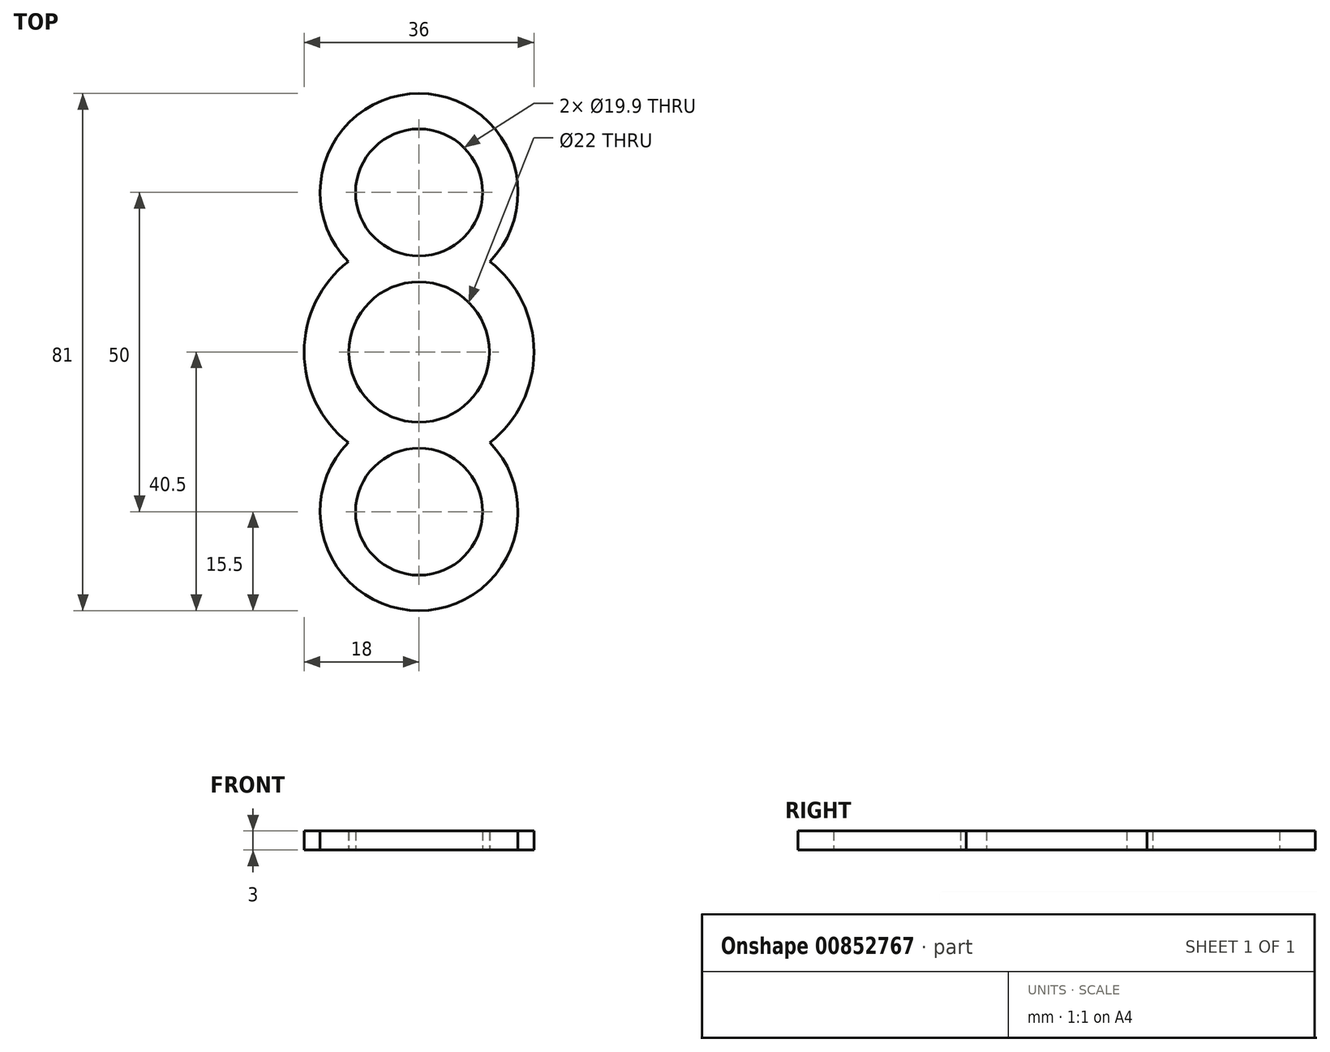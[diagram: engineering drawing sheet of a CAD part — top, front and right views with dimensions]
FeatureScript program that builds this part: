
annotation { "Feature Type Name" : "Feature", "Feature Type Description" : "" }
export const myFeature = defineFeature(function(context is Context, id is Id, definition is map)
    precondition{}
    {
        {
            var Q0;
            Q0=qCreatedBy(makeId("Top.planeOp"),FACE);
            var sketch = newSketch(context, id + "F0", { "sketchPlane" : qUnion([Q0])});
            skCircle(sketch, "E0", {"center": v(0, 0) * mm, "radius": 11 * mm});
            skCircle(sketch, "E1", {"center": v(0, 25) * mm, "radius": 9.95 * mm});
            skCircle(sketch, "E2", {"center": v(0, -25) * mm, "radius": 9.95 * mm});
            skArc(sketch, "E3", {"start": v(11.1, 14.18) * mm, "mid": v(0, 40.5) * mm, "end": v(-11.1, 14.18) * mm});
            skArc(sketch, "E4", {"start": v(-11.1, 14.18) * mm, "mid": v(-18, 0) * mm, "end": v(-11.1, -14.18) * mm});
            skArc(sketch, "E5", {"start": v(-11.1, -14.18) * mm, "mid": v(0, -40.5) * mm, "end": v(11.1, -14.18) * mm});
            skArc(sketch, "E6.trimOffspring", {"start": v(11.1, -14.18) * mm, "mid": v(18, 0) * mm, "end": v(11.1, 14.18) * mm});
            skSolve(sketch);
        }
        {
            var Q0;
            Q0 = qSketchRegion(id + "F0", true);
            extrude(context, id + "F1", {"entities" : qUnion([Q0]), "depth" : 3 * mm, "offsetDistance" : 25 * mm});
        }
    });
